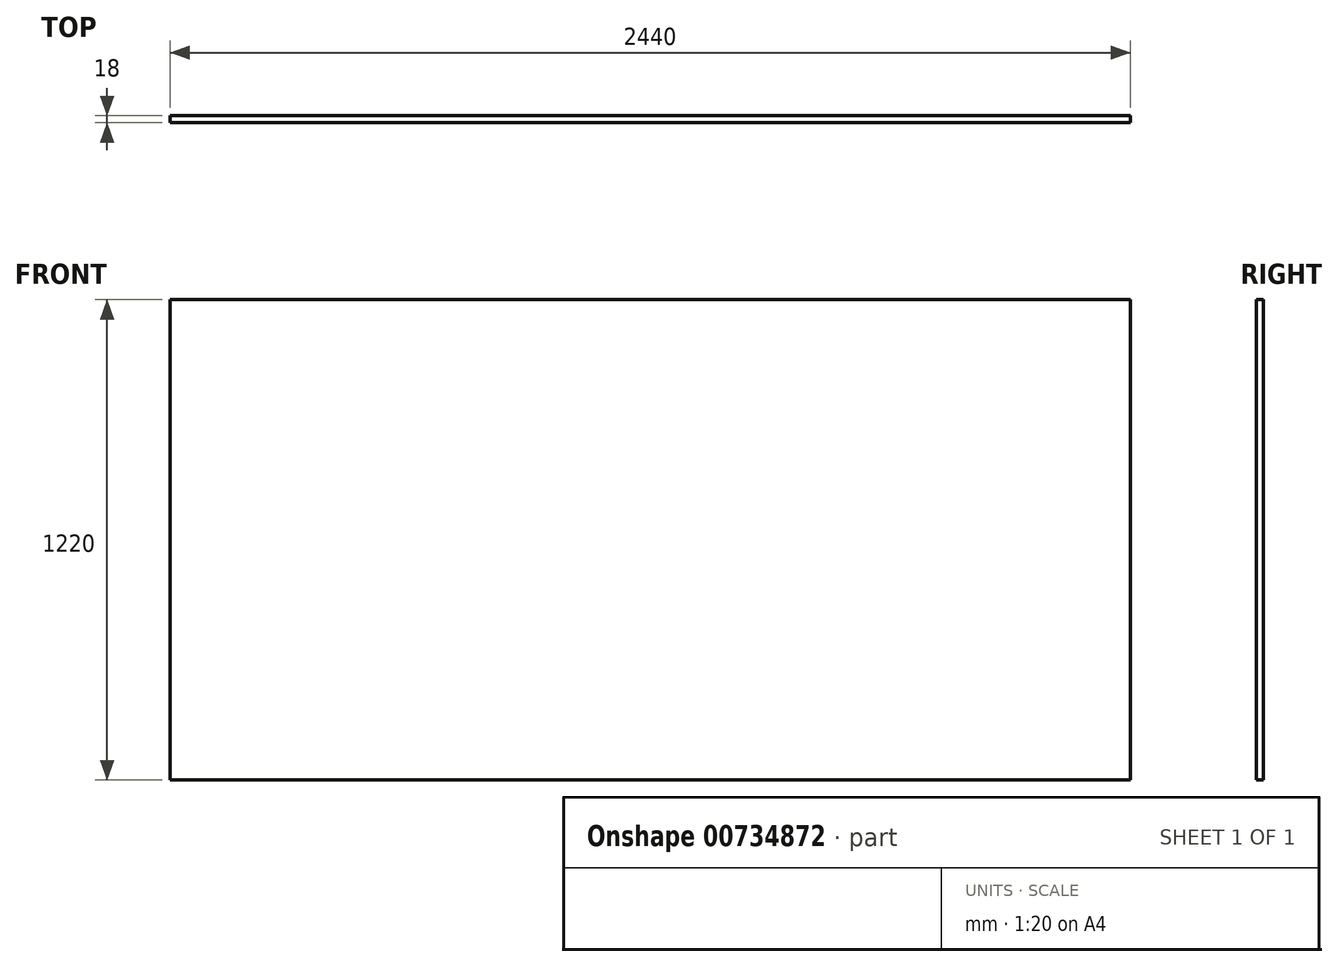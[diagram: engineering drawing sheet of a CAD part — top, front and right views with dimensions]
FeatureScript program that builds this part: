
annotation { "Feature Type Name" : "Feature", "Feature Type Description" : "" }
export const myFeature = defineFeature(function(context is Context, id is Id, definition is map)
    precondition{}
    {
        {
            var Q0;
            Q0=qCreatedBy(makeId("Front.planeOp"),FACE);
            var sketch = newSketch(context, id + "F0", { "sketchPlane" : qUnion([Q0])});
            skLineSegment(sketch, "E0.bottom", {"start": v(-1220, 610) * mm, "end": v(1220, 610) * mm});
            skLineSegment(sketch, "E0.top", {"start": v(-1220, -610) * mm, "end": v(1220, -610) * mm});
            skLineSegment(sketch, "E0.left", {"start": v(-1220, 610) * mm, "end": v(-1220, -610) * mm});
            skLineSegment(sketch, "E0.right", {"start": v(1220, 610) * mm, "end": v(1220, -610) * mm});
            skPoint(sketch, "E0.middle", {"position": v(0, 0) * mm});
            skSolve(sketch);
        }
        {
            var Q0;
            Q0=makeQuery(id+"F0.imprint","IMPRINT",FACE,{"disambiguationData":[TD([[makeQuery(id+"F0.imprint","IMPRINT",EDGE,{"derivedFrom":sQuery(id+"F0.wireOp",EDGE,"E0.bottom")}),-1.0]])]});
            extrude(context, id + "F1", {"entities" : qUnion([Q0]), "endBound" : BoundingType.SYMMETRIC, "depth" : 18 * mm, "offsetDistance" : 25.4 * mm});
        }
    });
